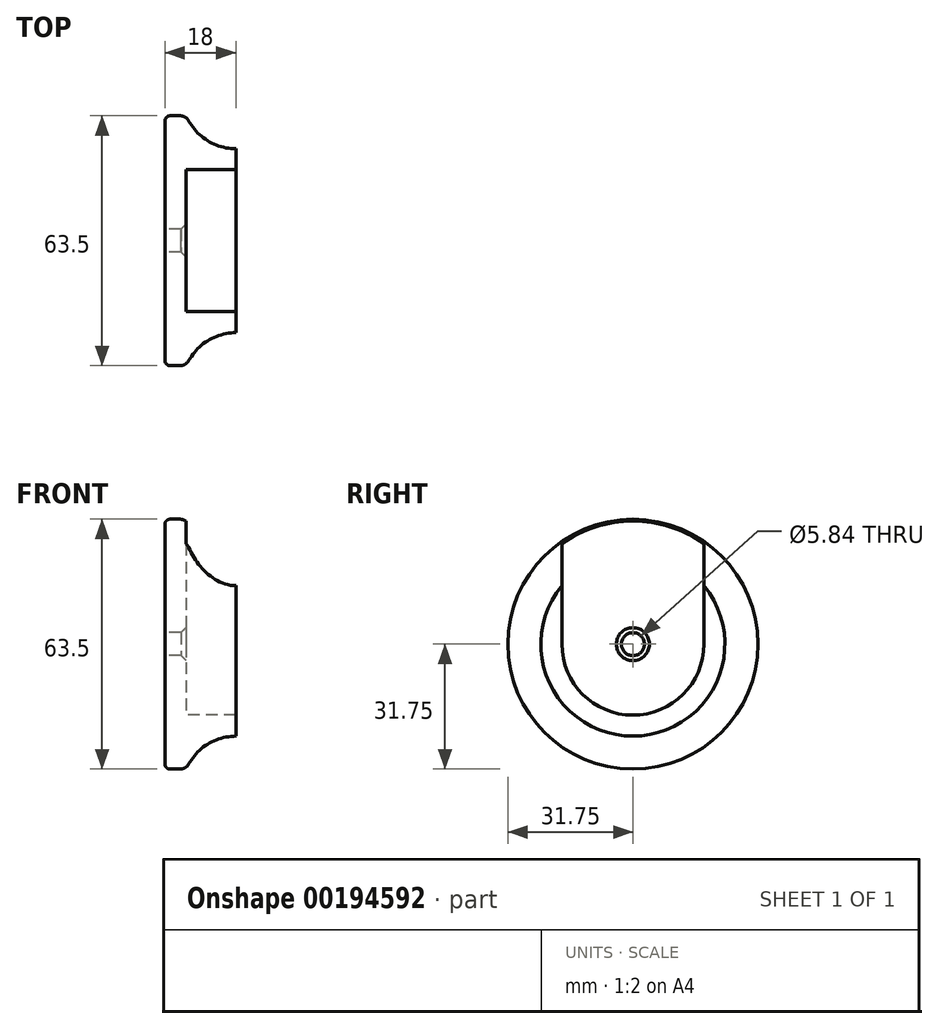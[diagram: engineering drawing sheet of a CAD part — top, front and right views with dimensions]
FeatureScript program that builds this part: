
annotation { "Feature Type Name" : "Feature", "Feature Type Description" : "" }
export const myFeature = defineFeature(function(context is Context, id is Id, definition is map)
    precondition{}
    {
        {
            var Q0;
            Q0=qCreatedBy(makeId("Front.planeOp"),FACE);
            var sketch = newSketch(context, id + "F0", { "sketchPlane" : qUnion([Q0])});
            skLineSegment(sketch, "E0", {"start": v(0, 2.92) * mm, "end": v(0, 30.48) * mm});
            skLineSegment(sketch, "E1", {"start": v(18, 23.37) * mm, "end": v(18, 18.03) * mm});
            skLineSegment(sketch, "E2", {"start": v(0, 0) * mm, "end": v(36.48, 0) * mm, "construction": true});
            skLineSegment(sketch, "E3", {"start": v(18, 18.03) * mm, "end": v(5.3, 18.03) * mm});
            skLineSegment(sketch, "E4", {"start": v(5.3, 18.03) * mm, "end": v(5.3, 4.2) * mm});
            skArc(sketch, "E5", {"start": v(6.03, 30.44) * mm, "mid": v(11.05, 25.27) * mm, "end": v(18, 23.37) * mm});
            skLineSegment(sketch, "E6", {"start": v(18, 23.37) * mm, "end": v(39.6, 23.37) * mm, "construction": true});
            skLineSegment(sketch, "E7", {"start": v(1.27, 31.75) * mm, "end": v(3.8, 31.75) * mm});
            skPoint(sketch, "E8.visualSharp", {"position": v(5.4, 31.75) * mm});
            skArc(sketch, "E8.filletArc", {"start": v(6.03, 30.44) * mm, "mid": v(5.1, 31.4) * mm, "end": v(3.8, 31.75) * mm});
            skPoint(sketch, "E9.visualSharp", {"position": v(0, 31.75) * mm});
            skArc(sketch, "E9.filletArc", {"start": v(1.27, 31.75) * mm, "mid": v(0.37, 31.38) * mm, "end": v(0, 30.48) * mm});
            skLineSegment(sketch, "E10", {"start": v(0, 2.92) * mm, "end": v(4.03, 2.92) * mm});
            skPoint(sketch, "E11.orphan", {"position": v(5.3, 0) * mm});
            skLineSegment(sketch, "E12", {"start": v(4.03, 2.92) * mm, "end": v(5.3, 4.2) * mm});
            skPoint(sketch, "E13.orphan", {"position": v(5.3, 2.92) * mm});
            skSolve(sketch);
        }
        {
            var Q0;
            Q0=qSketchRegion(id+"F0",true);
            var Q1;
            Q1=sQuery(id+"F0.wireOp",EDGE,"E2");
            revolve(context, id + "F1", {"entities" : qUnion([Q0]), "axis" : qUnion([Q1]), "revolveType" : RevolveType.FULL});
        }
        {
            var Q0;
            Q0=makeQuery(id+"F1.opRevolve","SWEPT_FACE",FACE,{"disambiguationData":[OSD([sQuery(id+"F0.wireOp",EDGE,"E1")])]});
            var sketch = newSketch(context, id + "F2", { "sketchPlane" : qUnion([Q0])});
            skLineSegment(sketch, "E14", {"start": v(-18.03, 0) * mm, "end": v(-18.03, 36.5) * mm});
            skArc(sketch, "E15.0", {"start": v(-18.03, 0) * mm, "mid": v(0, -18.03) * mm, "end": v(18.03, 0) * mm});
            skLineSegment(sketch, "E16", {"start": v(18.03, 0) * mm, "end": v(18.03, 36.5) * mm});
            skLineSegment(sketch, "E17", {"start": v(18.03, 36.5) * mm, "end": v(-18.03, 36.5) * mm});
            skSolve(sketch);
        }
        {
            var Q0;
            Q0 = qSketchRegion(id + "F2", true);
            var Q1;
            Q1=makeQuery(id+"F1.opRevolve","SWEPT_FACE",FACE,{"disambiguationData":[OSD([sQuery(id+"F0.wireOp",EDGE,"E4")])]});
            extrude(context, id + "F3", {"entities" : qUnion([Q0]), "operationType" : NewBodyOperationType.REMOVE, "endBound" : BoundingType.UP_TO_SURFACE, "oppositeDirection" : true, "endBoundEntityFace" : qUnion([Q1]), "depth" : 25.4 * mm});
        }
    });
